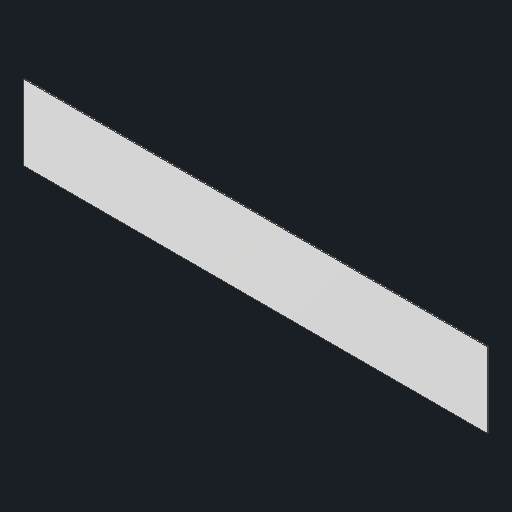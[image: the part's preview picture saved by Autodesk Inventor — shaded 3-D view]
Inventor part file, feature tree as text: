
AUTODESK INVENTOR PART (.ipt)
format: ipt  version: 2024.2 (Build 282272000, 272)  size: 79,360 bytes
history: native  units: in
note: dims shown in document units (in); Inventor stores cm internally (conversion verified against a paired STEP export)
features: extrude x1
ambient origin geometry x8: Origin, YZ Plane, XZ Plane, XY Plane, X Axis, Y Axis, Z Axis, Center Point
bodies: Solid1 (feature_tree)
feature tree (1):
  extrude  "Extrude1"  [1 undecoded]
note: 1 required parameter value undecoded (feature->parameter linkage not recoverable at this tier; creation-order binding heuristic only, values carry confidence <= 0.55)
